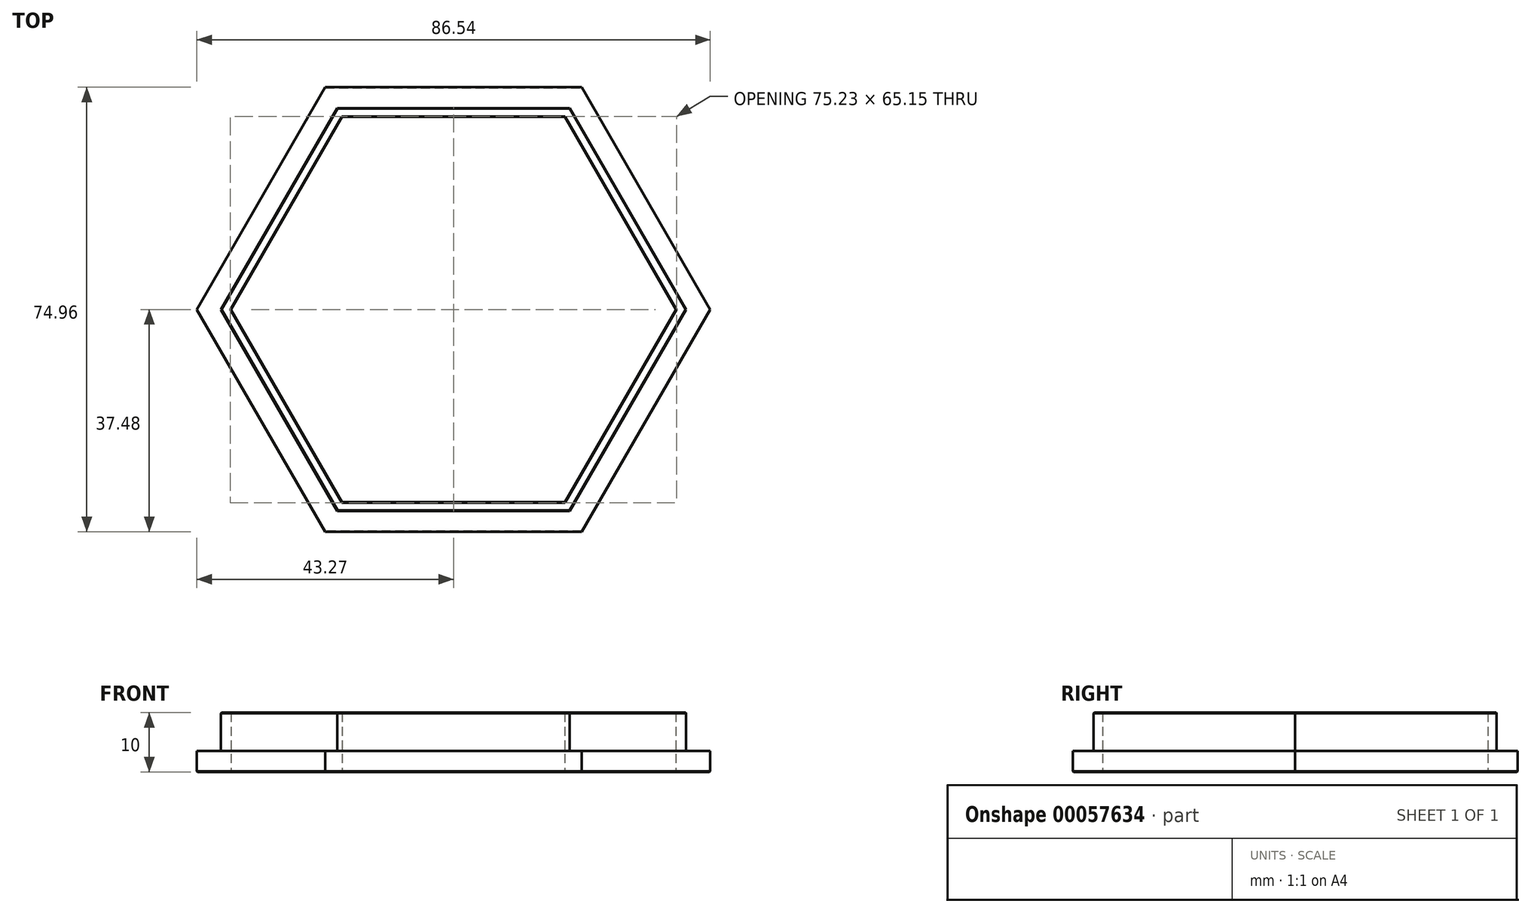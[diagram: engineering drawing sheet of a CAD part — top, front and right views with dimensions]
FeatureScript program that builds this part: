
annotation { "Feature Type Name" : "Feature", "Feature Type Description" : "" }
export const myFeature = defineFeature(function(context is Context, id is Id, definition is map)
    precondition{}
    {
        {
            var Q0;
            Q0=qCreatedBy(makeId("Top.planeOp"),FACE);
            var sketch = newSketch(context, id + "F0", { "sketchPlane" : qUnion([Q0])});
            skCircle(sketch, "E0.cCircle", {"center": v(0, 0) * mm, "radius": 32.48 * mm, "construction": true});
            skLineSegment(sketch, "E0.0", {"start": v(18.75, 32.48) * mm, "end": v(37.5, 0) * mm});
            skLineSegment(sketch, "E0.1", {"start": v(37.5, 0) * mm, "end": v(18.75, -32.48) * mm});
            skLineSegment(sketch, "E0.2", {"start": v(18.75, -32.48) * mm, "end": v(-18.75, -32.48) * mm});
            skLineSegment(sketch, "E0.3", {"start": v(-18.75, -32.48) * mm, "end": v(-37.5, 0) * mm});
            skLineSegment(sketch, "E0.4", {"start": v(-37.5, 0) * mm, "end": v(-18.75, 32.48) * mm});
            skLineSegment(sketch, "E0.5", {"start": v(-18.75, 32.48) * mm, "end": v(18.75, 32.48) * mm});
            skPoint(sketch, "E0.0.midPoint", {"position": v(28.12, 16.24) * mm});
            skCircle(sketch, "E1.cCircle", {"center": v(0, 0) * mm, "radius": 33.98 * mm, "construction": true});
            skLineSegment(sketch, "E1.0", {"start": v(19.62, 33.98) * mm, "end": v(39.23, 0) * mm});
            skLineSegment(sketch, "E1.1", {"start": v(39.23, 0) * mm, "end": v(19.62, -33.98) * mm});
            skLineSegment(sketch, "E1.2", {"start": v(19.62, -33.98) * mm, "end": v(-19.62, -33.98) * mm});
            skLineSegment(sketch, "E1.3", {"start": v(-19.62, -33.98) * mm, "end": v(-39.23, 0) * mm});
            skLineSegment(sketch, "E1.4", {"start": v(-39.23, 0) * mm, "end": v(-19.62, 33.98) * mm});
            skLineSegment(sketch, "E1.5", {"start": v(-19.62, 33.98) * mm, "end": v(19.62, 33.98) * mm});
            skPoint(sketch, "E1.0.midPoint", {"position": v(29.42, 16.99) * mm});
            skCircle(sketch, "E2.cCircle", {"center": v(0, 0) * mm, "radius": 37.48 * mm, "construction": true});
            skLineSegment(sketch, "E2.0", {"start": v(21.64, 37.48) * mm, "end": v(43.27, 0) * mm});
            skLineSegment(sketch, "E2.1", {"start": v(43.27, 0) * mm, "end": v(21.64, -37.48) * mm});
            skLineSegment(sketch, "E2.2", {"start": v(21.64, -37.48) * mm, "end": v(-21.64, -37.48) * mm});
            skLineSegment(sketch, "E2.3", {"start": v(-21.64, -37.48) * mm, "end": v(-43.27, 0) * mm});
            skLineSegment(sketch, "E2.4", {"start": v(-43.27, 0) * mm, "end": v(-21.64, 37.48) * mm});
            skLineSegment(sketch, "E2.5", {"start": v(-21.64, 37.48) * mm, "end": v(21.64, 37.48) * mm});
            skPoint(sketch, "E2.0.midPoint", {"position": v(32.46, 18.74) * mm});
            skSolve(sketch);
        }
        {
            var Q0;
            Q0=makeQuery(id+"F0.imprint","IMPRINT",FACE,{"disambiguationData":[TD([[makeQuery(id+"F0.imprint","IMPRINT",EDGE,{"derivedFrom":sQuery(id+"F0.wireOp",EDGE,"E0.0")}),1.0]])]});
            extrude(context, id + "F1", {"entities" : qUnion([Q0]), "depth" : 10 * mm});
        }
        {
            var Q0;
            Q0=makeQuery(id+"F0.imprint","IMPRINT",FACE,{"disambiguationData":[TD([[makeQuery(id+"F0.imprint","IMPRINT",EDGE,{"derivedFrom":sQuery(id+"F0.wireOp",EDGE,"E1.0")}),1.0]])]});
            extrude(context, id + "F2", {"entities" : qUnion([Q0]), "operationType" : NewBodyOperationType.ADD, "depth" : 3.5 * mm});
        }
        {
            var Q0;
            {var subQ0=sQuery(id+"F0.wireOp",EDGE,"E1.5");var subQ1=sQuery(id+"F0.wireOp",EDGE,"E1.4");var subQ2=sQuery(id+"F0.wireOp",EDGE,"E1.3");var subQ3=sQuery(id+"F0.wireOp",EDGE,"E1.2");var subQ4=sQuery(id+"F0.wireOp",EDGE,"E1.1");var subQ5=sQuery(id+"F0.wireOp",EDGE,"E1.0");Q0=makeQuery(id+"F2.boolean.opBoolean","MERGE",FACE,{"derivedFrom":[makeQuery(id+"F1.opExtrude","CAP_FACE",FACE,{"disambiguationData":[OSD([sQuery(id+"F0.wireOp",EDGE,"E0.0"),sQuery(id+"F0.wireOp",EDGE,"E0.1"),sQuery(id+"F0.wireOp",EDGE,"E0.2"),sQuery(id+"F0.wireOp",EDGE,"E0.3"),sQuery(id+"F0.wireOp",EDGE,"E0.4"),sQuery(id+"F0.wireOp",EDGE,"E0.5"),subQ5,subQ4,subQ3,subQ2,subQ1,subQ0])],"isStart":true}),makeQuery(id+"F2.opExtrude","CAP_FACE",FACE,{"disambiguationData":[OSD([subQ5,subQ4,subQ3,subQ2,subQ1,subQ0,sQuery(id+"F0.wireOp",EDGE,"E2.0"),sQuery(id+"F0.wireOp",EDGE,"E2.1"),sQuery(id+"F0.wireOp",EDGE,"E2.2"),sQuery(id+"F0.wireOp",EDGE,"E2.3"),sQuery(id+"F0.wireOp",EDGE,"E2.4"),sQuery(id+"F0.wireOp",EDGE,"E2.5")])],"isStart":true})]});}
            var Q1;
            Q1=makeQuery(id+"F1.opExtrude","CAP_FACE",FACE,{"disambiguationData":[OSD([sQuery(id+"F0.wireOp",EDGE,"E0.0"),sQuery(id+"F0.wireOp",EDGE,"E0.1"),sQuery(id+"F0.wireOp",EDGE,"E0.2"),sQuery(id+"F0.wireOp",EDGE,"E0.3"),sQuery(id+"F0.wireOp",EDGE,"E0.4"),sQuery(id+"F0.wireOp",EDGE,"E0.5"),sQuery(id+"F0.wireOp",EDGE,"E1.0"),sQuery(id+"F0.wireOp",EDGE,"E1.1"),sQuery(id+"F0.wireOp",EDGE,"E1.2"),sQuery(id+"F0.wireOp",EDGE,"E1.3"),sQuery(id+"F0.wireOp",EDGE,"E1.4"),sQuery(id+"F0.wireOp",EDGE,"E1.5")])],"isStart":false});
            chamfer(context, id + "F3", {"entities" : qUnion([Q0, Q1]), "width" : .1 * mm, "tangentPropagation" : true});
        }
    });
